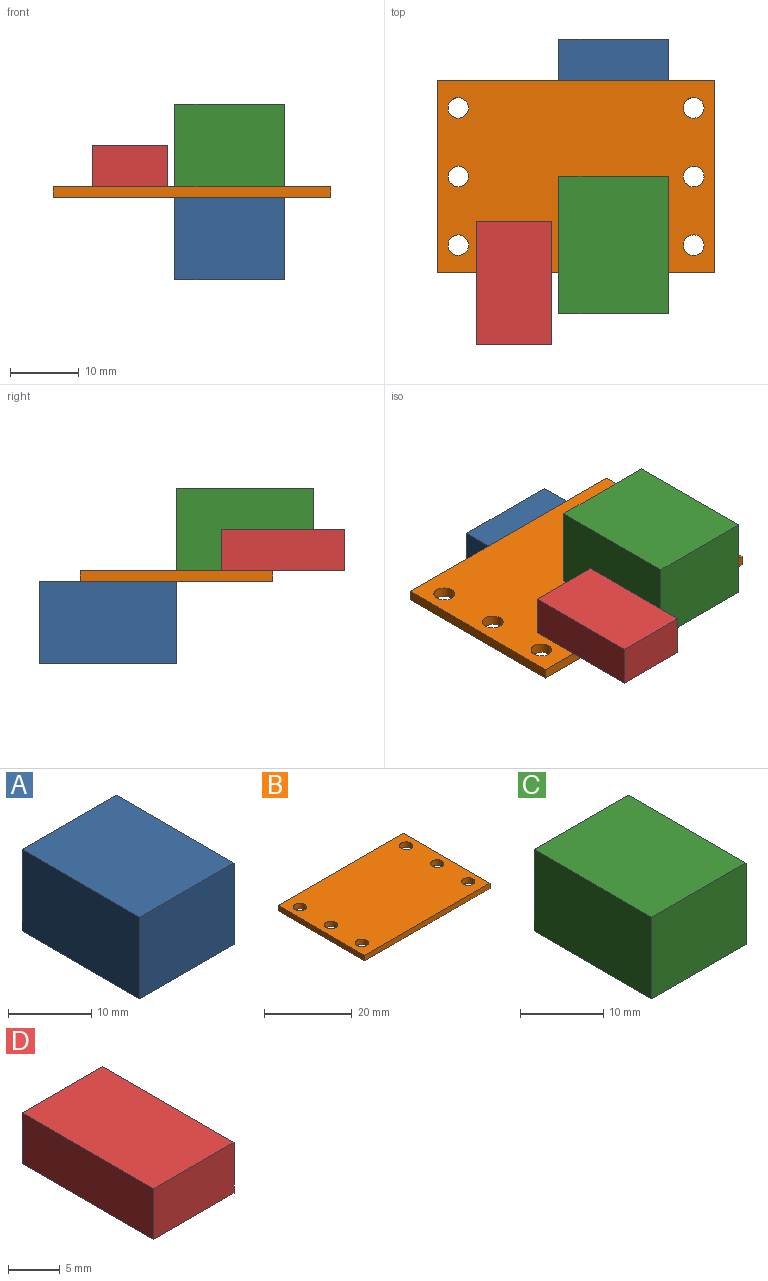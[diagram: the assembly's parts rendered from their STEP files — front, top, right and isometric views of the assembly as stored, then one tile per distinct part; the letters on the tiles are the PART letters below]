
ASSEMBLY  parts=4 mates=3
PART A: 6 faces, bbox 16x20x12 mm
  f0: plane 20x12mm, normal (1,0,0), area 240mm2, adj f1,f3,f4,f5
  f1: plane 16x12mm, normal (0,-1,0), area 192mm2, adj f0,f2,f4,f5
  f2: plane 20x12mm, normal (-1,0,0), area 240mm2, adj f1,f3,f4,f5
  f3: plane 16x12mm, normal (0,1,0), area 192mm2, adj f0,f2,f4,f5
  f4: plane 20x16mm, normal (0,0,-1), area 320mm2, adj f0,f1,f2,f3
  f5: plane 20x16mm, normal (0,0,1), area 320mm2, adj f0,f1,f2,f3
PART B: 12 faces, bbox 40.4x28x1.5 mm
  f0: plane 28x1.5mm, normal (1,0,0), area 42mm2, adj f1,f9,f10,f11
  f1: plane 40.4x1.5mm, normal (0,1,0), area 60.6mm2, adj f0,f2,f10,f11
  f2: plane 28x1.5mm, normal (-1,0,0), area 42mm2, adj f1,f9,f10,f11
  f3: cylinder r=1.5mm len=3mm, axis (0,0,-1), area 14.1mm2, adj f10,f11
  f4: cylinder r=1.5mm len=3mm, axis (0,0,-1), area 14.1mm2, adj f10,f11
  f5: cylinder r=1.5mm len=3mm, axis (0,0,-1), area 14.1mm2, adj f10,f11
  f6: cylinder r=1.5mm len=3mm, axis (0,0,-1), area 14.1mm2, adj f10,f11
  f7: cylinder r=1.5mm len=3mm, axis (0,0,-1), area 14.1mm2, adj f10,f11
  f8: cylinder r=1.5mm len=3mm, axis (0,0,-1), area 14.1mm2, adj f10,f11
  f9: plane 40.4x1.5mm, normal (0,-1,0), area 60.6mm2, adj f0,f2,f10,f11
  f10: plane 40.4x28mm, normal (0,0,1), area 1088.8mm2, adj f0,f1,f2,f3,f4,f5,f6,f7
  f11: plane 40.4x28mm, normal (0,0,-1), area 1088.8mm2, adj f0,f1,f2,f3,f4,f5,f6,f7
PART C: 6 faces, bbox 16x20x12 mm
  f0: plane 20x12mm, normal (-1,0,0), area 240mm2, adj f1,f3,f4,f5
  f1: plane 16x12mm, normal (0,-1,0), area 192mm2, adj f0,f2,f4,f5
  f2: plane 20x12mm, normal (1,0,0), area 240mm2, adj f1,f3,f4,f5
  f3: plane 16x12mm, normal (0,1,0), area 192mm2, adj f0,f2,f4,f5
  f4: plane 20x16mm, normal (0,0,1), area 320mm2, adj f0,f1,f2,f3
  f5: plane 20x16mm, normal (0,0,-1), area 320mm2, adj f0,f1,f2,f3
PART D: 6 faces, bbox 11x18x6 mm
  f0: plane 18x6mm, normal (1,0,0), area 108mm2, adj f1,f3,f4,f5
  f1: plane 11x6mm, normal (0,1,0), area 66mm2, adj f0,f2,f4,f5
  f2: plane 18x6mm, normal (-1,0,0), area 108mm2, adj f1,f3,f4,f5
  f3: plane 11x6mm, normal (0,-1,0), area 66mm2, adj f0,f2,f4,f5
  f4: plane 18x11mm, normal (0,0,1), area 198mm2, adj f0,f1,f2,f3
  f5: plane 18x11mm, normal (0,0,-1), area 198mm2, adj f0,f1,f2,f3
PLACE A at identity
PLACE B at identity fixed
PLACE C at identity
PLACE D at identity
MATE fastened A.f5 <-> B.f11  axis (0,0,1) through (-2.5,0,0)mm
MATE fastened C.f5 <-> B.f10  axis (0,0,-1) through (-2.5,0,1.5)mm
MATE fastened D.f5 <-> B.f10  axis (0,0,-1) through (-14.5,-6.5,1.5)mm
